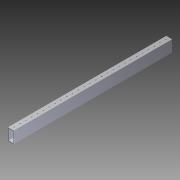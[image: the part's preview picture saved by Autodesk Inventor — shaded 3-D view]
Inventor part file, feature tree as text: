
AUTODESK INVENTOR PART (.ipt)
format: ipt  version: 2014 SP1 (Build 180222100, 222)  size: 773,120 bytes
history: native  units: in
note: dims shown in document units (in); Inventor stores cm internally (conversion verified against a paired STEP export)
features: other x2, extrude x2, sketch x2, imported_body x1
ambient origin geometry x8: Origin, YZ Plane, XZ Plane, XY Plane, X Axis, Y Axis, Z Axis, Center Point
bodies: Body1 (feature_tree)
feature tree (7):
  other  "Cut-Extrude2"
  other  "217-3453-STEP1"
  extrude  "Extrusion1"  Depth=15.9375in TaperAngle=0.0deg
  extrude  "Extrusion2"  [1 undecoded]
  imported_body  "Base1"
  sketch  "Sketch1"  dims[d0=15.9375in d1=0.0in d2=15.9375in d3=0.0in]
  sketch  "Sketch2"
note: 1 required parameter value undecoded (feature->parameter linkage not recoverable at this tier; creation-order binding heuristic only, values carry confidence <= 0.55)
